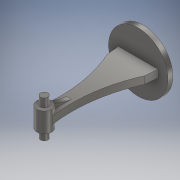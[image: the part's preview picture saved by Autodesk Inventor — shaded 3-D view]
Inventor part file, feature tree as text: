
AUTODESK INVENTOR PART (.ipt)
format: ipt  version: 2018 (Build 220112000, 112)  size: 170,496 bytes
history: native  units: mm
features: extrude x4, sketch x3, rib x1
ambient origin geometry x8: Origin, YZ Plane, XZ Plane, XY Plane, X Axis, Y Axis, Z Axis, Center Point
bodies: Solid1 (feature_tree)
feature tree (8):
  sketch  "Sketch1"  dims[d0=3.0mm d1=6.0mm]
  extrude  "Extrusion1"  Depth=6.0mm
  extrude  "Extrusion2"  Depth=2.0mm
  extrude  "Extrusion3"  Depth=8.0mm
  extrude  "Extrusion4"  Depth=2.0mm
  rib  "Rib1"
  sketch  "Sketch2"  dims[d2=40.0mm d3=2.0mm]
  sketch  "Sketch4"  dims[d4=8.0mm d5=8.0mm d7=5.0mm d8=7.5mm d9=7.5mm d10=60.0mm d11=60.0mm d13=7.164268mm d15=3.0mm d16=0.0mm d17=8.0mm d18=0.0mm d19=15.0mm d20=0.0mm d21=24.0mm d22=2.0mm d23=0.0mm d33=2.0mm d34=2.0mm d35=7.0mm d36=7.0mm d37=25.0mm d38=25.0mm d39=1.5mm d42=1.0mm d43=2.0mm d44=0.0mm d45=0.0mm d46=1.0mm d47=1.0mm]
